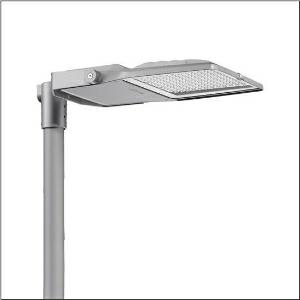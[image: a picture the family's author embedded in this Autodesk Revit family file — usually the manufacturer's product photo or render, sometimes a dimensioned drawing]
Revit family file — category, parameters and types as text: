
# Revit family: floodlight_fl_21_midi___pl43_5xa7785e2a3a_e2fe
name_source: partatom
category: Lighting Fixtures
units: mm (PartAtom-declared; Revit-internal decimal feet)

## family parameters
Cut with Voids When Loaded = No
Host = Face
Light Source = No
Part Type = Normal
Room Calculation Point = No
Round Connector Dimension = Use Diameter
Shared = No

## types (1)
- --- (1 x LED, 27640 lm, 212.4 W, 3000K)
    Apparent Load = 212 VA
    CIE Flux Codes = 27 78 99 100 100
    Color Rendering = 70
    Color Temperature = 3000K
    Default Elevation = 1800 mm
    Description = Floodlight FL 21 midi, floodlight, primary light control with lens, of PMMA, primary optical cover: protective disc, of toughened safety glass, transparent, light distribution: PL43, light emission: direct distribution, installation type: surface-mounted, LED, High Power LED, rated luminous flux: 27.640lm, luminous efficacy: 130lm/W, light colour: 730, colour temperature: 3000K, control gear: Smart Interface (Zhaga), control: flexible luminous flux parameterisation, time-dependent luminous flux control, constant luminous flux control, overheat protection, pre-setting: logarithmic dimming characteristic, with terminal, 6-pole, mains connection: 220..240V, AC, 50/60Hz, start of lifetime: 212W, end of service life: 231W, reduction: 95W, luminaire housing, of diecast aluminium, powder-coated, SITECO metallic grey (DB 702S), corrosivity category C5 mid according to DIN EN ISO 12944, suitable for swimming pools, chlorine-resistant, sealing non-destructively replaceable, please order mast flange separately, mast bracket, of steel, galvanised, powder-coated, SITECO metallic grey (DB 702S), Smart Interface above, protection rating (complete): IP66, insulation class (complete): insulation class II (safety insulation), certification: CE, ENEC, VDE, protection symbol: D, impact resistance: IK08, permissible operating ambient temperature: -20..+40°C, permissible operating ambient temperature for outdoor applications: -40..+50°C, standard: DIN EN 12944, LABS conformity tested according to VDMA 24364:2018-05, packaging unit: 1 piece

Light Distribution: PL43
    Height = 76 mm
    Lamp = 1 x LED
    Lamp Light Flux = 27640 lm
    Lamp Power = 212.4 W
    Lamp count = 1
    Length = 657 mm
    Luminous efficacy = 130 lm/W
    Manufacturer = Siteco
    ModVariant = No
    Model = 5XA7785E2A3A
    Number of Poles = 1
    OnlyDefault = Yes
    Power Factor = 1
    Product Name = Floodlight FL 21 midi | PL43
    Product group = floodlight | pylon annexe
    ProductGroupID = 6201
    Protection Class = Protection class II
    Protection Degree = IP 66
    RLX_Detail_Level = 1
    RLX_Emergency_Light_Flux = 0 lm
    RLX_Emergency_Type = 0
    RLX_Emergency_Type_DB = No
    RlxData = <blob elided: 153453 chars, md5=5ff4c58f>
    Socket = socket
    Standby Power = 0 W
    System Light Flux = 27640 lm
    System Power = 212 W
    Type Comments = factory setting: luminous flux: 100 % | dim-lin: 254 | 710 mA
    Type Image = l_1007123.jpg
    URL = http://relux.com
    VarID = @adj_176807
    Voltage = 0 V
    Weight = 0.00 kg
    Width = 442 mm

## geometry (parser evidence)
native form markers: Blend x4, Sweep x12
no freeform markers — native parametric forms only
